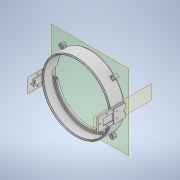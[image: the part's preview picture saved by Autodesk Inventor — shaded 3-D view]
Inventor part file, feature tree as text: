
AUTODESK INVENTOR PART (.ipt)
format: ipt  version: 2020.2 (Build 242310000, 310)  size: 923,136 bytes
history: native  units: mm
features: extrude x27, sketch x27, reference x21, other x8, plane x6, chamfer x3, pattern_circular x2, mirror x1, split x1, delete_face x1
ambient origin geometry x8: Origin, YZ Plane, XZ Plane, XY Plane, X Axis, Y Axis, Z Axis, Center Point
bodies: Solid1 (feature_tree), Solid2 (feature_tree), Solid3 (feature_tree)
feature tree (97):
  extrude  "Extrusion1"  Depth=205.0mm
  extrude  "Extrusion2"  Depth=40.0mm
  plane  "Work Plane4"
  extrude  "Extrusion3"  Depth=3.0mm TaperAngle=0.0deg
  extrude  "Extrusion4"  Depth=45.0mm
  extrude  "Extrusion6"  TaperAngle=0.0deg  [1 undecoded]
  extrude  "Extrusion8"  Depth=2.0mm
  chamfer  "Chamfer1"  Distance=20.0mm Angle=360.0deg
  pattern_circular  "Circular Pattern1"  Count=8  [1 undecoded]
  mirror  "Mirror1"
  plane  "Work Plane6"
  plane  "Work Plane8"
  extrude  "Extrusion15"  Depth=40.0mm
  extrude  "Extrusion16"  Depth=1.0mm
  extrude  "Extrusion17"  Depth=8.0mm
  extrude  "Extrusion20"  Depth=20.0mm TaperAngle=0.0deg
  chamfer  "Chamfer2"  Distance=5.0mm
  pattern_circular  "Circular Pattern2"  Count=2 Angle=360.0deg
  extrude  "Extrusion19"  Depth=191.666667mm
  extrude  "Extrusion21"  Depth=3.0mm TaperAngle=0.0deg
  extrude  "Extrusion22"  Depth=2.0mm
  extrude  "Extrusion23"  Depth=0.4mm
  extrude  "Extrusion24"  Depth=6.8mm
  plane  "Work Plane10"
  extrude  "Extrusion25"  TaperAngle=0.0deg  [1 undecoded]
  extrude  "Extrusion26"  TaperAngle=0.0deg  [1 undecoded]
  extrude  "Extrusion27"  Depth=3.0mm
  extrude  "Extrusion28"  Depth=3.0mm TaperAngle=0.0deg
  extrude  "Extrusion29"  Depth=3.0mm TaperAngle=0.0deg
  extrude  "Extrusion30"  Depth=3.0mm TaperAngle=0.0deg
  extrude  "Extrusion34"  Depth=2.0mm
  extrude  "Extrusion35"  Depth=2.0mm
  plane  "Work Plane11"
  extrude  "Extrusion36"  Depth=3.0mm TaperAngle=0.0deg
  extrude  "Extrusion37"  [1 undecoded]
  extrude  "Extrusion38"  Depth=3.0mm
  chamfer  "Chamfer3"  Distance=8.0mm
  split  "Split1"
  delete_face  "Delete Face1"
  extrude  "Extrusion39"  Depth=3.0mm
  sketch  "Sketch1"  dims[d0=215.0mm d1=205.0mm]
  sketch  "Sketch2"  dims[d2=40.0mm d3=0.0mm d4=208.633333mm]
  plane  "Work Plane3"
  sketch  "Sketch4"  dims[d5=211.366667mm d6=3.0mm d7=0.0mm]
  sketch  "Sketch5"  dims[d8=45.0mm d9=45.0mm]
  reference  "Reference1"
  sketch  "Sketch6"  dims[d10=3.0mm d11=0.0mm d12=0.0mm]
  sketch  "Sketch8"  dims[d13=2.0mm d14=0.0mm d17=0.1mm]
  reference  "Reference7"
  reference  "Reference8"
  reference  "Reference9"
  reference  "Reference10"
  sketch  "Sketch16"  dims[d18=1.9mm]
  sketch  "Sketch17"  dims[d19=0.0mm d23=20.0mm d24=360.0deg]
  reference  "Reference12"
  reference  "Reference13"
  sketch  "Sketch18"  dims[d26=0.1mm]
  sketch  "Sketch20"  dims[d27=1.0mm d28=0.0mm]
  sketch  "Sketch21"  dims[d29=2.0mm d30=2.0mm d31=45.0deg]
  sketch  "Sketch22"  dims[d67=30.2mm]
  sketch  "Sketch23"  dims[d68=41.0mm d69=80.0mm]
  reference  "Reference14"
  reference  "Reference15"
  sketch  "Sketch24"  dims[d70=40.0mm d71=20.5mm]
  sketch  "Sketch25"  dims[d72=215.0mm d73=0.0mm d74=1.0mm]
  reference  "Reference16"
  reference  "Reference17"
  sketch  "Sketch26"  dims[d75=4.0mm d76=8.0mm]
  reference  "Reference18"
  reference  "Reference19"
  sketch  "Sketch27"  dims[d77=26.0mm d78=20.0mm d79=0.0mm]
  reference  "Reference20"
  reference  "Reference21"
  sketch  "Sketch28"  dims[d80=10.0mm d83=5.0mm d84=0.0mm]
  sketch  "Sketch29"  dims[d85=0.0mm]
  reference  "Reference22"
  reference  "Reference23"
  reference  "Reference24"
  reference  "Reference25"
  sketch  "Sketch30"  dims[d86=2.5mm d87=0.0mm d97=20.0mm d98=360.0deg]
  reference  "Reference26"
  reference  "Reference27"
  sketch  "Sketch31"  dims[d100=215.0mm d101=0.0mm d102=191.666667mm]
  sketch  "Sketch35"  dims[d103=198.333333mm d104=3.0mm d105=0.0mm]
  sketch  "Sketch36"  dims[d106=2.0mm d107=2.0mm d108=45.0deg d110=20.0mm]
  sketch  "Sketch39"  dims[d111=72.5mm d112=0.0mm d114=0.4mm]
  sketch  "Sketch40"  dims[d115=6.0mm d116=6.8mm]
  sketch  "Sketch41"  dims[d117=6.8mm d118=0.0mm]
  sketch  "Sketch42"  dims[d119=0.0mm d120=0.0mm d121=6.0mm d122=4.0mm d123=0.0mm d124=7.5mm d125=0.0mm d126=3.0mm d127=0.0mm d128=2.0mm d129=2.0mm d130=6.0mm d131=0.0mm d132=-7.0mm d133=16.0mm d134=8.0mm d135=0.5mm d136=40.0mm d137=30.2mm d138=3.0mm d139=22.0mm d140=0.0mm d141=2.0mm d142=2.0mm d143=10.0mm d144=0.0mm d145=5.0mm d146=5.0mm d147=4.0mm d148=0.0mm d149=100.0mm d150=0.0mm d151=57.0mm d153=10.0mm d154=1.8mm d155=0.0mm d156=10.0mm d157=0.0mm d158=3.0mm d159=3.0mm d160=5.0mm d161=0.0mm d162=1.5mm d163=0.0mm d176=28.0mm d177=20.0mm d178=6.0mm d179=4.0mm d180=30.0mm d181=1.0mm d182=0.0mm d183=1.0mm d184=0.0mm d185=12.0mm d186=14.0mm d187=4.0mm d188=40.0mm d190=360.0deg d192=20.0mm d193=0.0mm d194=7.0mm d195=40.0mm d197=360.0deg d199=4.0mm d200=0.0mm d201=8.0mm d202=40.0mm d204=360.0deg d206=5.0mm d207=0.0mm d208=3.0mm d209=2.0mm d210=45.0deg d211=1.6mm d212=1.6mm d213=1.6mm d214=1.6mm d215=1.6mm d216=3.0mm d217=0.0mm d88=0.872665mm]
  other  "<userpath>\OneDrive\Apps\0011_VentControlValve\Assembly.iam"
  other  "Assembly.iam"
  other  "Base:1"
  other  "<userpath>\OneDrive\Apps\0011_VentControlValve\Drawings\Assembly.iam"
  other  "Butterfly Valve:1"
  other  "limitSwitch:2"
  other  "limitSwitch:1"
  other  "motor+Gearbox:1"
note: 5 required parameter values undecoded (feature->parameter linkage not recoverable at this tier; creation-order binding heuristic only, values carry confidence <= 0.55)
